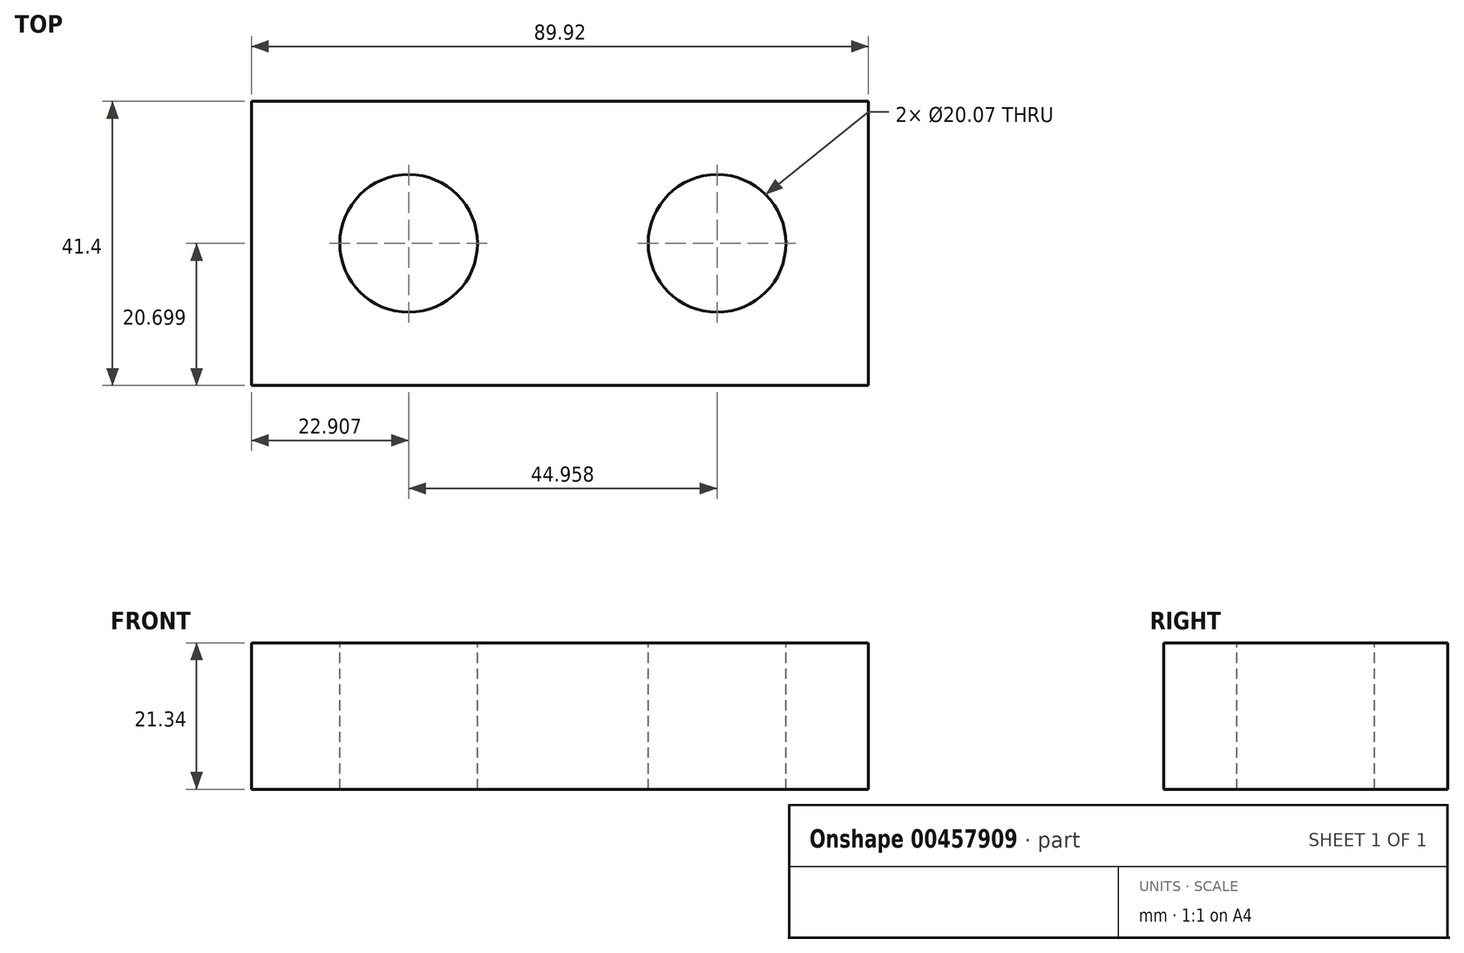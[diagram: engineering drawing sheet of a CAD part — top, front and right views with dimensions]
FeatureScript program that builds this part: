
annotation { "Feature Type Name" : "Feature", "Feature Type Description" : "" }
export const myFeature = defineFeature(function(context is Context, id is Id, definition is map)
    precondition{}
    {
        {
            var Q0;
            Q0=qCreatedBy(makeId("Front.planeOp"),FACE);
            var sketch = newSketch(context, id + "F0", { "sketchPlane" : qUnion([Q0])});
            skLineSegment(sketch, "E0.bottom", {"start": v(-45.8, 16.58) * mm, "end": v(44.11, 16.58) * mm});
            skLineSegment(sketch, "E0.top", {"start": v(-45.8, 37.92) * mm, "end": v(44.11, 37.92) * mm});
            skLineSegment(sketch, "E0.left", {"start": v(-45.8, 16.58) * mm, "end": v(-45.8, 37.92) * mm});
            skLineSegment(sketch, "E0.right", {"start": v(44.11, 16.58) * mm, "end": v(44.11, 37.92) * mm});
            skSolve(sketch);
        }
        {
            var Q0;
            Q0 = qSketchRegion(id + "F0", true);
            extrude(context, id + "F1", {"entities" : qUnion([Q0]), "depth" : 41.4 * mm});
        }
        {
            var Q0;
            Q0=makeQuery(id+"F1.opExtrude","SWEPT_FACE",FACE,{"disambiguationData":[OSD([sQuery(id+"F0.wireOp",EDGE,"E0.top")])]});
            var sketch = newSketch(context, id + "F2", { "sketchPlane" : qUnion([Q0])});
            skLineSegment(sketch, "E1", {"start": v(-0.85, 0) * mm, "end": v(-0.85, -41.4) * mm, "construction": true});
            skLineSegment(sketch, "E2", {"start": v(-45.8, -20.7) * mm, "end": v(0, -20.7) * mm, "construction": true});
            skLineSegment(sketch, "E3", {"start": v(0, -20.7) * mm, "end": v(44.11, -20.7) * mm, "construction": true});
            skCircle(sketch, "E4", {"center": v(-22.9, -20.7) * mm, "radius": 10.03 * mm});
            skCircle(sketch, "E5", {"center": v(22.06, -20.7) * mm, "radius": 10.03 * mm});
            skSolve(sketch);
        }
        {
            var Q0;
            Q0=makeQuery(id+"F2.imprint","IMPRINT",FACE,{"disambiguationData":[TD([[makeQuery(id+"F2.imprint","IMPRINT",EDGE,{"derivedFrom":sQuery(id+"F2.wireOp",EDGE,"E4")}),1.0]])]});
            var Q1;
            Q1=makeQuery(id+"F2.imprint","IMPRINT",FACE,{"disambiguationData":[TD([[makeQuery(id+"F2.imprint","IMPRINT",EDGE,{"derivedFrom":sQuery(id+"F2.wireOp",EDGE,"E5")}),1.0]])]});
            var Q2;
            Q2=sQuery(id+"F2.wireOp",EDGE,"E4");
            extrude(context, id + "F3", {"entities" : qUnion([Q0, Q1]), "operationType" : NewBodyOperationType.REMOVE, "surfaceEntities" : qUnion([Q2]), "endBound" : BoundingType.THROUGH_ALL, "oppositeDirection" : true, "depth" : 25.4 * mm});
        }
    });
